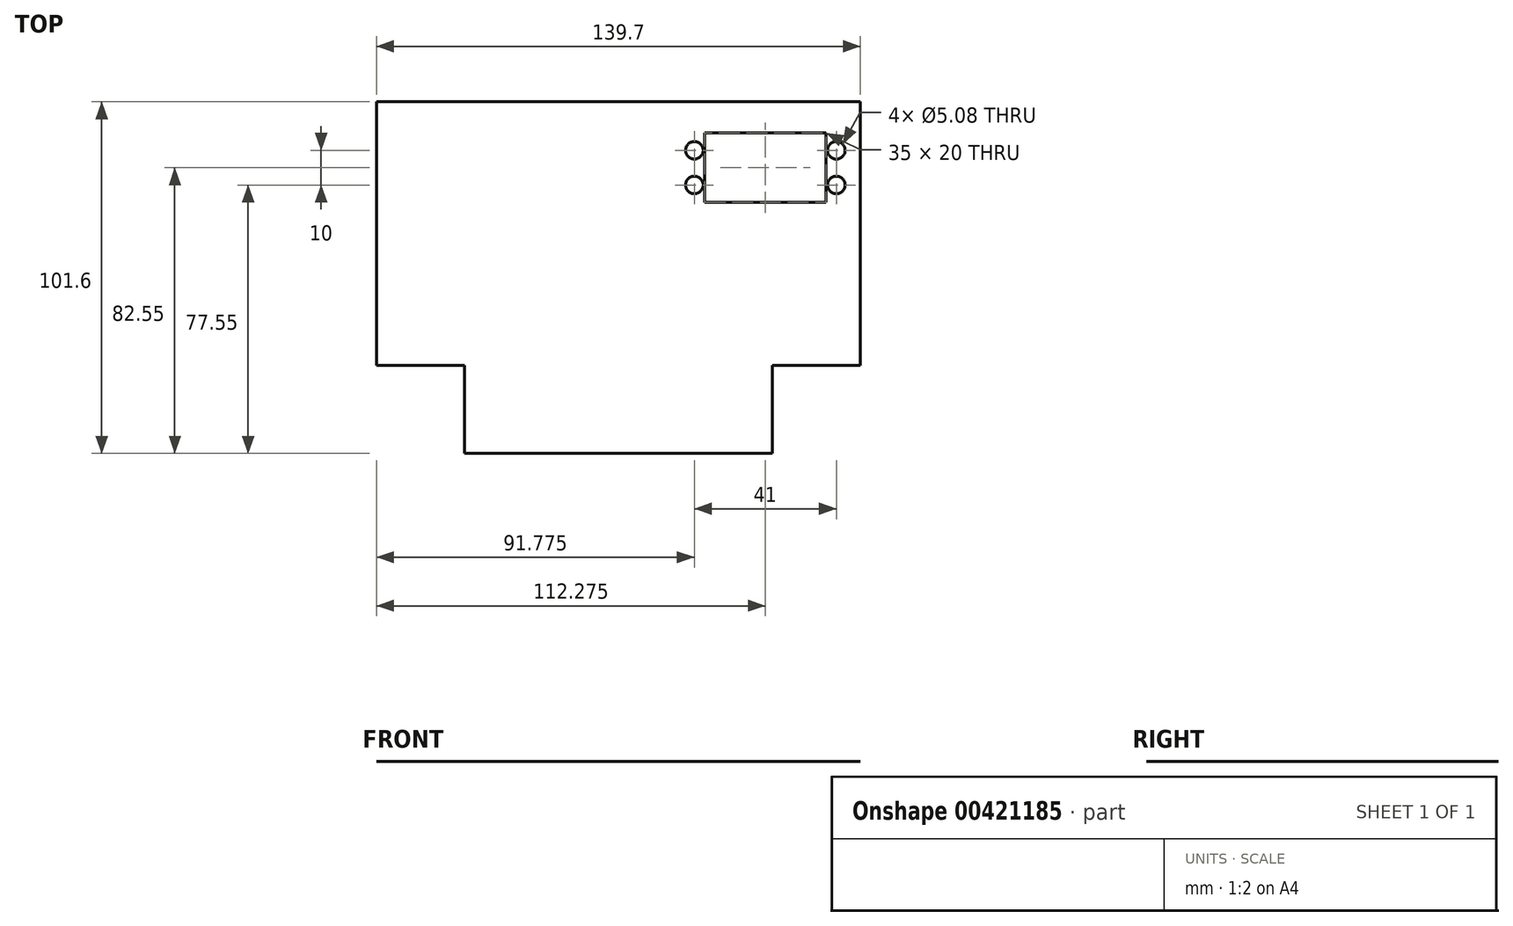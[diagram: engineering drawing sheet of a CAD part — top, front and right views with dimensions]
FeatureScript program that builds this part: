
annotation { "Feature Type Name" : "Feature", "Feature Type Description" : "" }
export const myFeature = defineFeature(function(context is Context, id is Id, definition is map)
    precondition{}
    {
        {
            var Q0;
            Q0=qCreatedBy(makeId("Top.planeOp"),FACE);
            var sketch = newSketch(context, id + "F0", { "sketchPlane" : qUnion([Q0])});
            skLineSegment(sketch, "E0", {"start": v(0, 101.6) * mm, "end": v(139.7, 101.6) * mm});
            skLineSegment(sketch, "E1", {"start": v(25.4, 0) * mm, "end": v(114.3, 0) * mm});
            skLineSegment(sketch, "E2.left", {"start": v(25.4, 0) * mm, "end": v(25.4, 25.4) * mm});
            skLineSegment(sketch, "E2.right", {"start": v(114.3, 0) * mm, "end": v(114.3, 25.4) * mm});
            skLineSegment(sketch, "E3", {"start": v(0, 101.6) * mm, "end": v(0, 25.4) * mm});
            skLineSegment(sketch, "E4", {"start": v(139.7, 25.4) * mm, "end": v(139.7, 101.6) * mm});
            skLineSegment(sketch, "E5", {"start": v(139.7, 25.4) * mm, "end": v(114.3, 25.4) * mm});
            skLineSegment(sketch, "E6", {"start": v(25.4, 25.4) * mm, "end": v(0, 25.4) * mm});
            skLineSegment(sketch, "E7", {"start": v(104.78, 92.55) * mm, "end": v(129.78, 92.55) * mm});
            skLineSegment(sketch, "E8", {"start": v(104.78, 72.55) * mm, "end": v(129.78, 72.55) * mm});
            skLineSegment(sketch, "E9", {"start": v(129.78, 72.55) * mm, "end": v(129.78, 92.55) * mm});
            skLineSegment(sketch, "E10.bottom", {"start": v(94.78, 92.55) * mm, "end": v(129.78, 92.55) * mm});
            skLineSegment(sketch, "E10.top", {"start": v(94.78, 72.55) * mm, "end": v(129.78, 72.55) * mm});
            skLineSegment(sketch, "E10.left", {"start": v(94.78, 92.55) * mm, "end": v(94.78, 72.55) * mm});
            skLineSegment(sketch, "E10.right", {"start": v(129.78, 92.55) * mm, "end": v(129.78, 72.55) * mm});
            skCircle(sketch, "E11", {"center": v(132.78, 87.55) * mm, "radius": 2.54 * mm});
            skCircle(sketch, "E12", {"center": v(132.78, 77.55) * mm, "radius": 2.54 * mm});
            skCircle(sketch, "E13", {"center": v(91.78, 77.55) * mm, "radius": 2.54 * mm});
            skCircle(sketch, "E14", {"center": v(91.78, 87.55) * mm, "radius": 2.54 * mm});
            skSolve(sketch);
        }
        {
            var Q0;
            Q0=makeQuery(id+"F0.imprint","IMPRINT",FACE,{"disambiguationData":[TD([[makeQuery(id+"F0.imprint","IMPRINT",EDGE,{"derivedFrom":sQuery(id+"F0.wireOp",EDGE,"E0")}),-1.0]])]});
            extrude(context, id + "F1", {"entities" : qUnion([Q0]), "depth" : 1 / 203.2 * mm});
        }
    });
